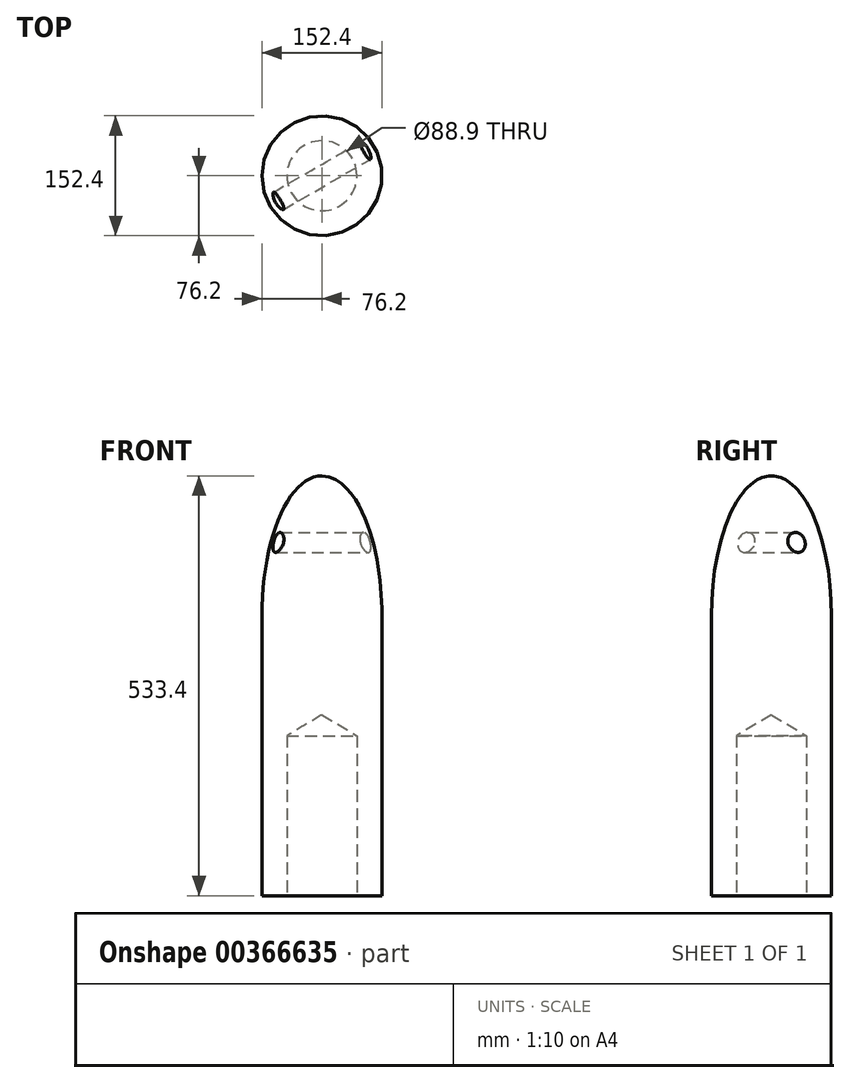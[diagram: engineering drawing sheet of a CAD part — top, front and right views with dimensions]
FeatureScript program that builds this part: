
annotation { "Feature Type Name" : "Feature", "Feature Type Description" : "" }
export const myFeature = defineFeature(function(context is Context, id is Id, definition is map)
    precondition{}
    {
        {
            var Q0;
            Q0=qCreatedBy(makeId("Front.planeOp"),FACE);
            var sketch = newSketch(context, id + "F0", { "sketchPlane" : qUnion([Q0])});
            skEllipticalArc(sketch, "E0", {});
            skPoint(sketch, "E1", {"position": v(-76.2, 27.68) * mm});
            skPoint(sketch, "E2", {"position": v(76.2, 27.68) * mm});
            skLineSegment(sketch, "E3", {"start": v(-76.2, 27.68) * mm, "end": v(-76.2, -327.92) * mm});
            skLineSegment(sketch, "E4", {"start": v(76.2, 27.68) * mm, "end": v(76.2, -327.92) * mm});
            skLineSegment(sketch, "E5", {"start": v(76.2, -327.92) * mm, "end": v(-76.2, -327.92) * mm});
            skLineSegment(sketch, "E6", {"start": v(0, -327.92) * mm, "end": v(0, 205.48) * mm});
            const initialGuessF0  = {"E0": [0, 0.027678270701239793, 0, 1, 0.1778, 0.0762, 4.71238898038469, 1.5707963267948966]};
            skSetInitialGuess(sketch, initialGuessF0);
            skSolve(sketch);
        }
        {
            var Q0;
            {var subQ2=sQuery(id+"F0.wireOp",EDGE,"E3");Q0=makeQuery(id+"F0.imprint","IMPRINT",FACE,{"disambiguationData":[TD([[makeQuery(id+"F0.imprint","IMPRINT",EDGE,{"derivedFrom":subQ2}),1.0]])]});}
            var Q1;
            Q1=sQuery(id+"F0.wireOp",EDGE,"E6");
            revolve(context, id + "F1", {"entities" : qUnion([Q0]), "axis" : qUnion([Q1]), "revolveType" : RevolveType.FULL, "oppositeDirection" : true});
        }
        {
            var Q0;
            Q0=makeQuery(id+"F1.opRevolve","SWEPT_FACE",FACE,{"disambiguationData":[OSD([sQuery(id+"F0.wireOp",EDGE,"E5")])]});
            var sketch = newSketch(context, id + "F2", { "sketchPlane" : qUnion([Q0])});
            skCircle(sketch, "E7", {"center": v(0, 0) * mm, "radius": 44.45 * mm});
            skSolve(sketch);
        }
        {
            var Q0;
            Q0=sQuery(id+"F2.wireOp",VERTEX,"E7.center");
            var Q1;
            Q1=makeQuery(id+"F1.opRevolve","SWEPT_BODY",BODY,{"disambiguationData":[OSD([sQuery(id+"F0.wireOp",EDGE,"E0"),sQuery(id+"F0.wireOp",EDGE,"E3"),sQuery(id+"F0.wireOp",EDGE,"E5"),sQuery(id+"F0.wireOp",EDGE,"E6")])]});
            hole(context, id + "F3", {"style" : HoleStyle.SIMPLE, "endStyle" : HoleEndStyle.BLIND, "holeDiameter" : 88.9 * mm, "holeDepth" : 203.2 * mm, "isTappedThrough" : true, "tappedDepth" : 12.7 * mm, "tapClearance" : 3, "startFromSketch" : true, "locations" : qUnion([Q0]), "scope" : qUnion([Q1])});
        }
        {
            var Q0;
            Q0=makeQuery(id+"F1.opRevolve","SWEPT_FACE",FACE,{"disambiguationData":[OSD([sQuery(id+"F0.wireOp",EDGE,"E0")])]});
            cPlane(context, id + "F4", {"entities" : qUnion([Q0]), "cplaneType" : CPlaneType.LINE_ANGLE, "offset" : 25.4 * mm, "angle" : 30 * degree, "width" : 152.4 * mm, "height" : 152.4 * mm});
        }
        {
            var Q0;
            Q0=qCreatedBy(id+"F4.planeOp",FACE);
            var sketch = newSketch(context, id + "F5", { "sketchPlane" : qUnion([Q0])});
            skPoint(sketch, "E8", {"position": v(0, 120.9) * mm});
            skSolve(sketch);
        }
        {
            var Q0;
            Q0=sQuery(id+"F5.wireOp",VERTEX,"E8");
            var Q1;
            Q1=makeQuery(id+"F1.opRevolve","SWEPT_BODY",BODY,{"disambiguationData":[OSD([sQuery(id+"F0.wireOp",EDGE,"E0"),sQuery(id+"F0.wireOp",EDGE,"E3"),sQuery(id+"F0.wireOp",EDGE,"E5"),sQuery(id+"F0.wireOp",EDGE,"E6")])]});
            hole(context, id + "F6", {"style" : HoleStyle.C_BORE, "endStyle" : HoleEndStyle.THROUGH, "holeDiameter" : 25.4 * mm, "cBoreDiameter" : 25.4 * mm, "cBoreDepth" : 6.35 * mm, "isTappedThrough" : true, "tappedDepth" : 12.7 * mm, "tapClearance" : 3, "startFromSketch" : true, "locations" : qUnion([Q0]), "scope" : qUnion([Q1])});
        }
        {
            var Q0;
            Q0=sQuery(id+"F5.wireOp",VERTEX,"E8");
            var Q1;
            Q1=makeQuery(id+"F1.opRevolve","SWEPT_BODY",BODY,{"disambiguationData":[OSD([sQuery(id+"F0.wireOp",EDGE,"E0"),sQuery(id+"F0.wireOp",EDGE,"E3"),sQuery(id+"F0.wireOp",EDGE,"E5"),sQuery(id+"F0.wireOp",EDGE,"E6")])]});
            hole(context, id + "F7", {"style" : HoleStyle.C_BORE, "endStyle" : HoleEndStyle.THROUGH, "oppositeDirection" : true, "holeDiameter" : 25.4 * mm, "cBoreDiameter" : 25.4 * mm, "cBoreDepth" : 25.4 * mm, "isTappedThrough" : true, "tappedDepth" : 12.7 * mm, "tapClearance" : 3, "startFromSketch" : true, "locations" : qUnion([Q0]), "scope" : qUnion([Q1])});
        }
    });
